# Revit family: 32QMR,QMR-A,QMR-B_SET_231217_1
name_source: partatom
category: 통신 장치
units: mm (PartAtom-declared; Revit-internal decimal feet)

## family parameters
OmniClass 번호 = 23.85.10.14.24
OmniClass 제목 = Video Monitors
공유 = 아니오
로드될 때 보이드를 사용하여 절단 = 아니오
룸 계산 점 = 아니오
부품 유형 = 보통
원형 커넥터 치수 = 지름 사용
작업 기준면 기반 = 아니오
주석 방향을 유지합니다. = 아니오
항상 수직 = 예

## types (3) — shared parameters
Active Display Area = 698.4(H) x 392.85(V)
Bezel Width (mm) = 8.8
Brightness (Typ.) = 400
Color Gamut = 72%
Contrast Ratio (Typ.) = 5000:1
Diagonal Size (Class) = 32  [stored 0.104987 ft]
Diagonal Size (Measured) = 31.5
Dimension Package (mm) = 812 x 513 x 120
Dimension Set (mm) = 725.1 x 419.6 x 34.6
Dimension Set Depth (mm) = 34.6  [stored 0.113517 ft]
Dimension Set Height (mm) = 419.6  [stored 1.37664 ft]
Dimension Set Width (mm) = 725.1  [stored 2.37894 ft]
Display Colors = 16.7M(True Display), 1.07B(Ditherd 10bit)
Dynamic C/R = MEGA
Environment = ENERGY STAR 8.0, EPEAT
External Control = RS232C(in/out) thru stereo jack, RJ45
External Sensor = IR
H-Scanning Frequency = 30 ~ 81kHZ
Haze = 2%
Input Audio = Stereo Mini Jack, HDMI/Audio(Common)
Input HDCP = HDCP2.2
Input RGB = Display Port 1.2 (1)
Input USB = USB 2.0 x 2
Internal Clock Speed = 1.7GHz
Internal Graphics = Graphic resolution : 1920x1080, Output resolution : 1920x1080 (Scale up from graphic processing result.)
Internal IO Ports = USB 2.0
Internal Main Memory Interface = 2.5GB, LPDDR4 1.5GHz 64bit
Internal Multimedia = Video Decoder  : MPEG-1/2/4, H.263, H.264/AVC, UHD H.264/AVC,  VC-1, AVS+, HEVC, JPEG, PNG, VP8, VP9  *Audio Decoder : AC3 (DD), MPEG
Internal On-Chip Cache Memory = L1 Instruction Cache : 48KB, L1 Data Cache : 32KB, L2 Cache : 2MB
Internal Operating System = Tizen 4.0 (VDLinux)
Internal Processor = Cortex A72 1.7GHz Quad-Core CPU
Internal Storage (FDM) = 8GB (3.88GB Occupied by O/S, 4.12GB Available)
Key = FHD Signage Display Slim & Light Signage with Built-in MagicInfo S6, SSSP 6.0
Maximum Pixel Frequency = 594MHz
Operation Hour = 24/7
Optional Mount = WMN4070SG (Land Only), WMN750ME
Optional Specialty = CML400XK
Optional Stand = STN-L3240F
Orientation = Landscape / Portrait
Output Audio = Stereo mini Jack
Pixel Pitch (mm) = 0.360(H) x 0.360(V)
Power Consumption Max [W/h] = 72
Power Consumption Rating [W/h] = 65
Power Consumption Sleep mode = 0.5
Power Consumption Typical [W/h] = 44
Power Supply = AC100 - 240V, 50/60 Hz
Power Type = Internal
Relative Humidity = 10~80%
Resolution = FHD (1920 x 1080)
Response Time (GtoG) = 8ms
Safety = 60950-1
Screen = Samsung Electronics Screen
Security = 802.1 x (WPA2 Enterprise) : EAP-TLS, EAP-TTLS, EAP-PEAP
Sound = Built in Speaker(10W + 10W)
Stand Type = Foot Stand (Optional)
Temperature = 0℃ ~ 40℃
Type = Edge LED BLU
V-Scanning Frequency = 48 ~ 75HZ
VESA Mount = 200 x 200
Viewing Angle(H/V) = 178/178
Weight Package (kg) = 8
Weight Set (kg) = 5.7
제조업체 = Samsung Electronics Co., Ltd.
조합 코드 = E1020500
키노트 = 11 52 00

## per-type parameters (varying)
| type | EMC | Input Video | Output RGB | Power Consumption BTU(Max) |
| UHD Signage QM32R | Class B | HDMI 2.0(2) | HDMI 2.0 (Loop-out) | 245.5 |
| UHD Signage QM32R-A | Class B(TBD) | HDMI 2.0 (2) |  | 245.7 |
| UHD Signage QM32R-B | Class B(TBD) | HDMI 2.0 (2) |  | 245.7 |

note: column(s) folded — value = type name in every type: 모델

note: [stored X ft] marks values corroborated as IEEE doubles in the binary element streams (Revit-internal decimal feet)
